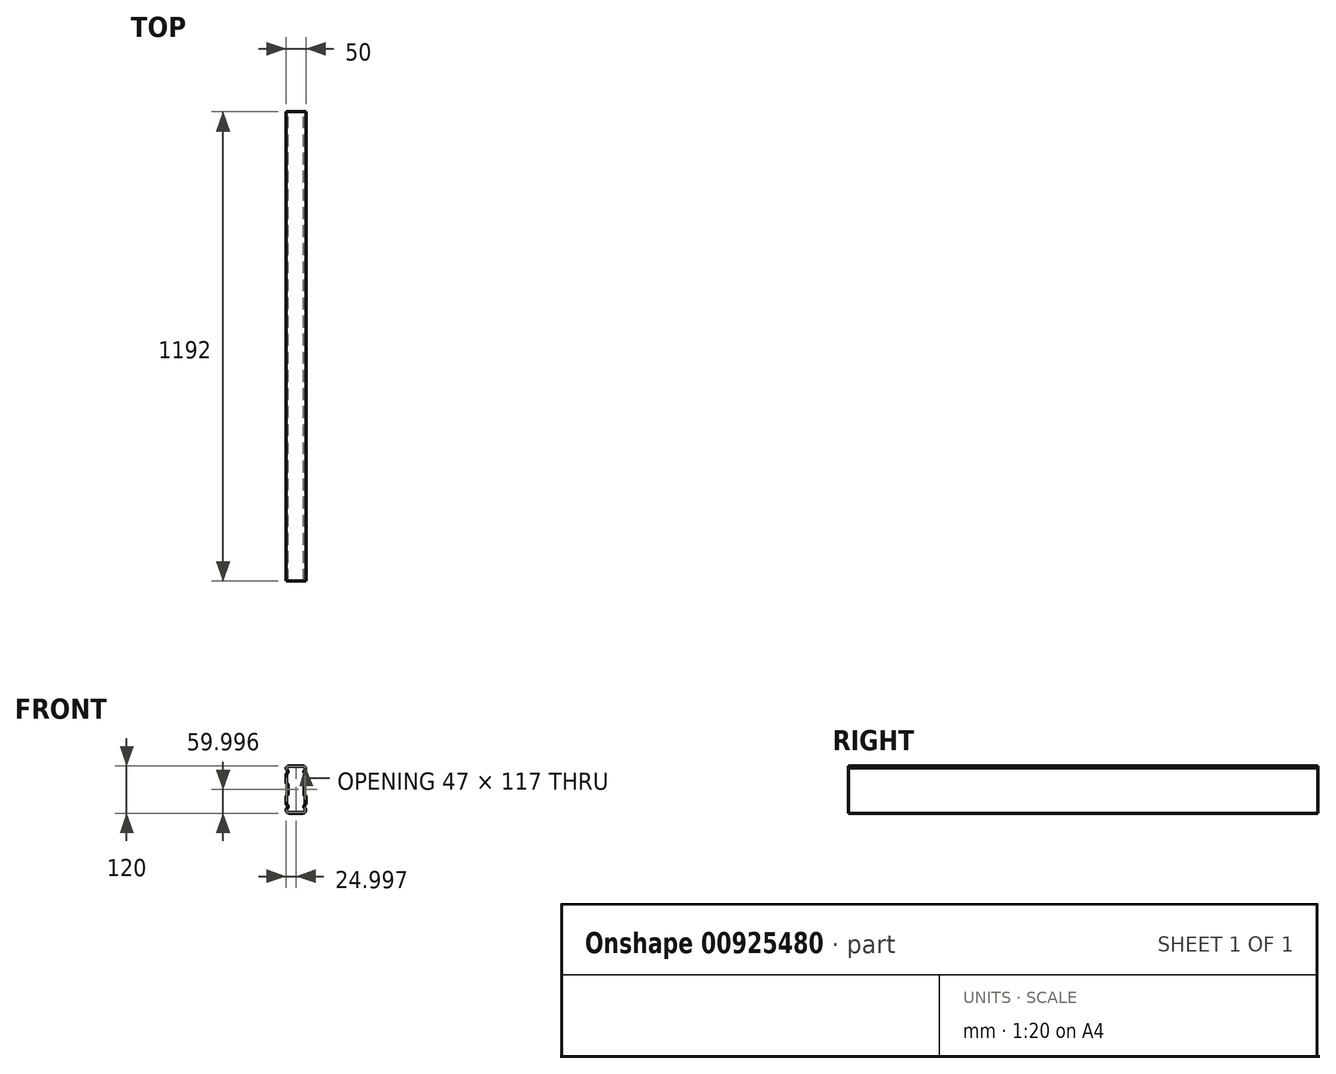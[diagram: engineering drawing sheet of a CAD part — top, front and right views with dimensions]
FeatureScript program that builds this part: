
annotation { "Feature Type Name" : "Feature", "Feature Type Description" : "" }
export const myFeature = defineFeature(function(context is Context, id is Id, definition is map)
    precondition{}
    {
        {
            var Q0;
            Q0=qCreatedBy(makeId("Front.planeOp"),FACE);
            var sketch = newSketch(context, id + "F0", { "sketchPlane" : qUnion([Q0])});
            skArc(sketch, "E0.filletArc", {"start": v(-76.42, 85.7) * mm, "mid": v(-80.94, 84.2) * mm, "end": v(-83.63, 80.26) * mm});
            skArc(sketch, "E1.filletArc", {"start": v(-83.63, -26.8) * mm, "mid": v(-81.44, -32.1) * mm, "end": v(-76.13, -34.3) * mm});
            skArc(sketch, "E2", {"start": v(-80.87, -20.14) * mm, "mid": v(-82.91, -23.2) * mm, "end": v(-83.63, -26.8) * mm});
            skArc(sketch, "E3", {"start": v(-80.03, -17.47) * mm, "mid": v(-80.97, -14.8) * mm, "end": v(-82.7, -12.57) * mm});
            skArc(sketch, "E4.filletArc", {"start": v(-80.87, -20.14) * mm, "mid": v(-80.12, -18.91) * mm, "end": v(-80.03, -17.47) * mm});
            skLineSegment(sketch, "E5", {"start": v(-83.63, -10.39) * mm, "end": v(-83.63, 8.51) * mm});
            skLineSegment(sketch, "E6", {"start": v(-83.63, 10.7) * mm, "end": v(-83.63, 10.7) * mm});
            skLineSegment(sketch, "E7", {"start": v(-80.63, 13.7) * mm, "end": v(-80.63, 37.7) * mm});
            skLineSegment(sketch, "E8", {"start": v(-83.63, 40.7) * mm, "end": v(-83.63, 40.7) * mm});
            skArc(sketch, "E9.filletArc", {"start": v(-82.13, 11.1) * mm, "mid": v(-81.03, 12.2) * mm, "end": v(-80.63, 13.7) * mm});
            skPoint(sketch, "E10.visualSharp", {"position": v(-83.63, 10.7) * mm});
            skArc(sketch, "E10.filletArc", {"start": v(-82.13, 11.1) * mm, "mid": v(-83.23, 10.01) * mm, "end": v(-83.63, 8.51) * mm});
            skArc(sketch, "E11.filletArc", {"start": v(-80.63, 37.7) * mm, "mid": v(-81.03, 39.2) * mm, "end": v(-82.13, 40.3) * mm});
            skPoint(sketch, "E12.visualSharp", {"position": v(-83.63, 40.7) * mm});
            skArc(sketch, "E12.filletArc", {"start": v(-83.63, 42.9) * mm, "mid": v(-83.23, 41.4) * mm, "end": v(-82.13, 40.3) * mm});
            skArc(sketch, "E13.filletArc", {"start": v(-83.63, -10.39) * mm, "mid": v(-83.39, -11.58) * mm, "end": v(-82.7, -12.57) * mm});
            skArc(sketch, "E14", {"start": v(-83.63, 80.26) * mm, "mid": v(-82.92, 76.67) * mm, "end": v(-80.89, 73.63) * mm});
            skArc(sketch, "E15", {"start": v(-82.72, 66.04) * mm, "mid": v(-81.02, 68.28) * mm, "end": v(-80.07, 70.92) * mm});
            skArc(sketch, "E16.filletArc", {"start": v(-80.07, 70.92) * mm, "mid": v(-80.14, 72.38) * mm, "end": v(-80.89, 73.63) * mm});
            skArc(sketch, "E17.filletArc", {"start": v(-82.72, 66.04) * mm, "mid": v(-83.4, 65.05) * mm, "end": v(-83.63, 63.88) * mm});
            skLineSegment(sketch, "E18", {"start": v(-83.63, 42.9) * mm, "end": v(-83.63, 63.88) * mm});
            skArc(sketch, "E19.MirrorCS", {"start": v(-33.63, 42.9) * mm, "mid": v(-34.03, 41.4) * mm, "end": v(-35.13, 40.3) * mm});
            skArc(sketch, "E20.MirrorCS", {"start": v(-36.63, 37.7) * mm, "mid": v(-36.23, 39.2) * mm, "end": v(-35.13, 40.3) * mm});
            skArc(sketch, "E21.MirrorCS", {"start": v(-35.13, 11.1) * mm, "mid": v(-36.23, 12.2) * mm, "end": v(-36.63, 13.7) * mm});
            skArc(sketch, "E22.MirrorCS", {"start": v(-35.13, 11.1) * mm, "mid": v(-34.03, 10.01) * mm, "end": v(-33.63, 8.51) * mm});
            skArc(sketch, "E23.MirrorCS", {"start": v(-34.54, 66.04) * mm, "mid": v(-33.87, 65.05) * mm, "end": v(-33.63, 63.88) * mm});
            skArc(sketch, "E24.MirrorCS", {"start": v(-36.4, -20.14) * mm, "mid": v(-37.15, -18.91) * mm, "end": v(-37.24, -17.47) * mm});
            skArc(sketch, "E25.MirrorCS", {"start": v(-33.63, -10.39) * mm, "mid": v(-33.88, -11.58) * mm, "end": v(-34.57, -12.57) * mm});
            skArc(sketch, "E26.MirrorCS", {"start": v(-37.2, 70.92) * mm, "mid": v(-37.13, 72.38) * mm, "end": v(-36.38, 73.63) * mm});
            skArc(sketch, "E27.MirrorCS", {"start": v(-34.54, 66.04) * mm, "mid": v(-36.24, 68.28) * mm, "end": v(-37.2, 70.92) * mm});
            skArc(sketch, "E28.MirrorCS", {"start": v(-37.24, -17.47) * mm, "mid": v(-36.3, -14.8) * mm, "end": v(-34.57, -12.57) * mm});
            skArc(sketch, "E29.MirrorCS", {"start": v(-33.63, 80.26) * mm, "mid": v(-34.35, 76.67) * mm, "end": v(-36.38, 73.63) * mm});
            skArc(sketch, "E30.MirrorCS", {"start": v(-36.4, -20.14) * mm, "mid": v(-34.35, -23.2) * mm, "end": v(-33.63, -26.8) * mm});
            skArc(sketch, "E31.MirrorCS", {"start": v(-33.63, -26.8) * mm, "mid": v(-35.83, -32.1) * mm, "end": v(-41.13, -34.3) * mm});
            skArc(sketch, "E32.MirrorCS", {"start": v(-40.85, 85.7) * mm, "mid": v(-36.33, 84.2) * mm, "end": v(-33.63, 80.26) * mm});
            skLineSegment(sketch, "E33.MirrorCS", {"start": v(-33.63, 42.9) * mm, "end": v(-33.63, 63.88) * mm});
            skLineSegment(sketch, "E34.MirrorCS", {"start": v(-33.63, -10.39) * mm, "end": v(-33.63, 8.51) * mm});
            skLineSegment(sketch, "E35.MirrorCS", {"start": v(-36.63, 13.7) * mm, "end": v(-36.63, 37.7) * mm});
            skLineSegment(sketch, "E36", {"start": v(-76.42, 85.7) * mm, "end": v(-40.85, 85.7) * mm});
            skLineSegment(sketch, "E37", {"start": v(-76.13, -34.3) * mm, "end": v(-41.13, -34.3) * mm});
            skSolve(sketch);
        }
        {
            var Q0;
            Q0=makeQuery(id+"F0.imprint","IMPRINT",FACE,{"disambiguationData":[TD([[makeQuery(id+"F0.imprint","IMPRINT",EDGE,{"derivedFrom":sQuery(id+"F0.wireOp",EDGE,"E0.filletArc")}),1.0]])]});
            extrude(context, id + "F1", {"entities" : qUnion([Q0]), "depth" : 1192 * mm, "offsetDistance" : 25 * mm});
        }
        {
            var Q0;
            Q0=makeQuery(id+"F1.opExtrude","CAP_FACE",FACE,{"disambiguationData":[OSD([sQuery(id+"F0.wireOp",EDGE,"E0.filletArc"),sQuery(id+"F0.wireOp",EDGE,"E1.filletArc"),sQuery(id+"F0.wireOp",EDGE,"E2"),sQuery(id+"F0.wireOp",EDGE,"E3"),sQuery(id+"F0.wireOp",EDGE,"E4.filletArc"),sQuery(id+"F0.wireOp",EDGE,"E5"),sQuery(id+"F0.wireOp",EDGE,"E7"),sQuery(id+"F0.wireOp",EDGE,"E9.filletArc"),sQuery(id+"F0.wireOp",EDGE,"E10.filletArc"),sQuery(id+"F0.wireOp",EDGE,"E11.filletArc"),sQuery(id+"F0.wireOp",EDGE,"E12.filletArc"),sQuery(id+"F0.wireOp",EDGE,"E13.filletArc"),sQuery(id+"F0.wireOp",EDGE,"E14"),sQuery(id+"F0.wireOp",EDGE,"E15"),sQuery(id+"F0.wireOp",EDGE,"E16.filletArc"),sQuery(id+"F0.wireOp",EDGE,"E17.filletArc"),sQuery(id+"F0.wireOp",EDGE,"E18"),sQuery(id+"F0.wireOp",EDGE,"E19.MirrorCS"),sQuery(id+"F0.wireOp",EDGE,"E20.MirrorCS"),sQuery(id+"F0.wireOp",EDGE,"E21.MirrorCS"),sQuery(id+"F0.wireOp",EDGE,"E22.MirrorCS"),sQuery(id+"F0.wireOp",EDGE,"E23.MirrorCS"),sQuery(id+"F0.wireOp",EDGE,"E24.MirrorCS"),sQuery(id+"F0.wireOp",EDGE,"E25.MirrorCS"),sQuery(id+"F0.wireOp",EDGE,"E26.MirrorCS"),sQuery(id+"F0.wireOp",EDGE,"E27.MirrorCS"),sQuery(id+"F0.wireOp",EDGE,"E28.MirrorCS"),sQuery(id+"F0.wireOp",EDGE,"E29.MirrorCS"),sQuery(id+"F0.wireOp",EDGE,"E30.MirrorCS"),sQuery(id+"F0.wireOp",EDGE,"E31.MirrorCS"),sQuery(id+"F0.wireOp",EDGE,"E32.MirrorCS"),sQuery(id+"F0.wireOp",EDGE,"E33.MirrorCS"),sQuery(id+"F0.wireOp",EDGE,"E34.MirrorCS"),sQuery(id+"F0.wireOp",EDGE,"E35.MirrorCS"),sQuery(id+"F0.wireOp",EDGE,"E36"),sQuery(id+"F0.wireOp",EDGE,"E37")])],"isStart":true});
            var Q1;
            Q1=makeQuery(id+"F1.opExtrude","CAP_FACE",FACE,{"disambiguationData":[OSD([sQuery(id+"F0.wireOp",EDGE,"E0.filletArc"),sQuery(id+"F0.wireOp",EDGE,"E1.filletArc"),sQuery(id+"F0.wireOp",EDGE,"E2"),sQuery(id+"F0.wireOp",EDGE,"E3"),sQuery(id+"F0.wireOp",EDGE,"E4.filletArc"),sQuery(id+"F0.wireOp",EDGE,"E5"),sQuery(id+"F0.wireOp",EDGE,"E7"),sQuery(id+"F0.wireOp",EDGE,"E9.filletArc"),sQuery(id+"F0.wireOp",EDGE,"E10.filletArc"),sQuery(id+"F0.wireOp",EDGE,"E11.filletArc"),sQuery(id+"F0.wireOp",EDGE,"E12.filletArc"),sQuery(id+"F0.wireOp",EDGE,"E13.filletArc"),sQuery(id+"F0.wireOp",EDGE,"E14"),sQuery(id+"F0.wireOp",EDGE,"E15"),sQuery(id+"F0.wireOp",EDGE,"E16.filletArc"),sQuery(id+"F0.wireOp",EDGE,"E17.filletArc"),sQuery(id+"F0.wireOp",EDGE,"E18"),sQuery(id+"F0.wireOp",EDGE,"E19.MirrorCS"),sQuery(id+"F0.wireOp",EDGE,"E20.MirrorCS"),sQuery(id+"F0.wireOp",EDGE,"E21.MirrorCS"),sQuery(id+"F0.wireOp",EDGE,"E22.MirrorCS"),sQuery(id+"F0.wireOp",EDGE,"E23.MirrorCS"),sQuery(id+"F0.wireOp",EDGE,"E24.MirrorCS"),sQuery(id+"F0.wireOp",EDGE,"E25.MirrorCS"),sQuery(id+"F0.wireOp",EDGE,"E26.MirrorCS"),sQuery(id+"F0.wireOp",EDGE,"E27.MirrorCS"),sQuery(id+"F0.wireOp",EDGE,"E28.MirrorCS"),sQuery(id+"F0.wireOp",EDGE,"E29.MirrorCS"),sQuery(id+"F0.wireOp",EDGE,"E30.MirrorCS"),sQuery(id+"F0.wireOp",EDGE,"E31.MirrorCS"),sQuery(id+"F0.wireOp",EDGE,"E32.MirrorCS"),sQuery(id+"F0.wireOp",EDGE,"E33.MirrorCS"),sQuery(id+"F0.wireOp",EDGE,"E34.MirrorCS"),sQuery(id+"F0.wireOp",EDGE,"E35.MirrorCS"),sQuery(id+"F0.wireOp",EDGE,"E36"),sQuery(id+"F0.wireOp",EDGE,"E37")])],"isStart":false});
            shell(context, id + "F2", {"entities" : qUnion([Q0, Q1]), "thickness" : 1.5 * mm});
        }
    });
